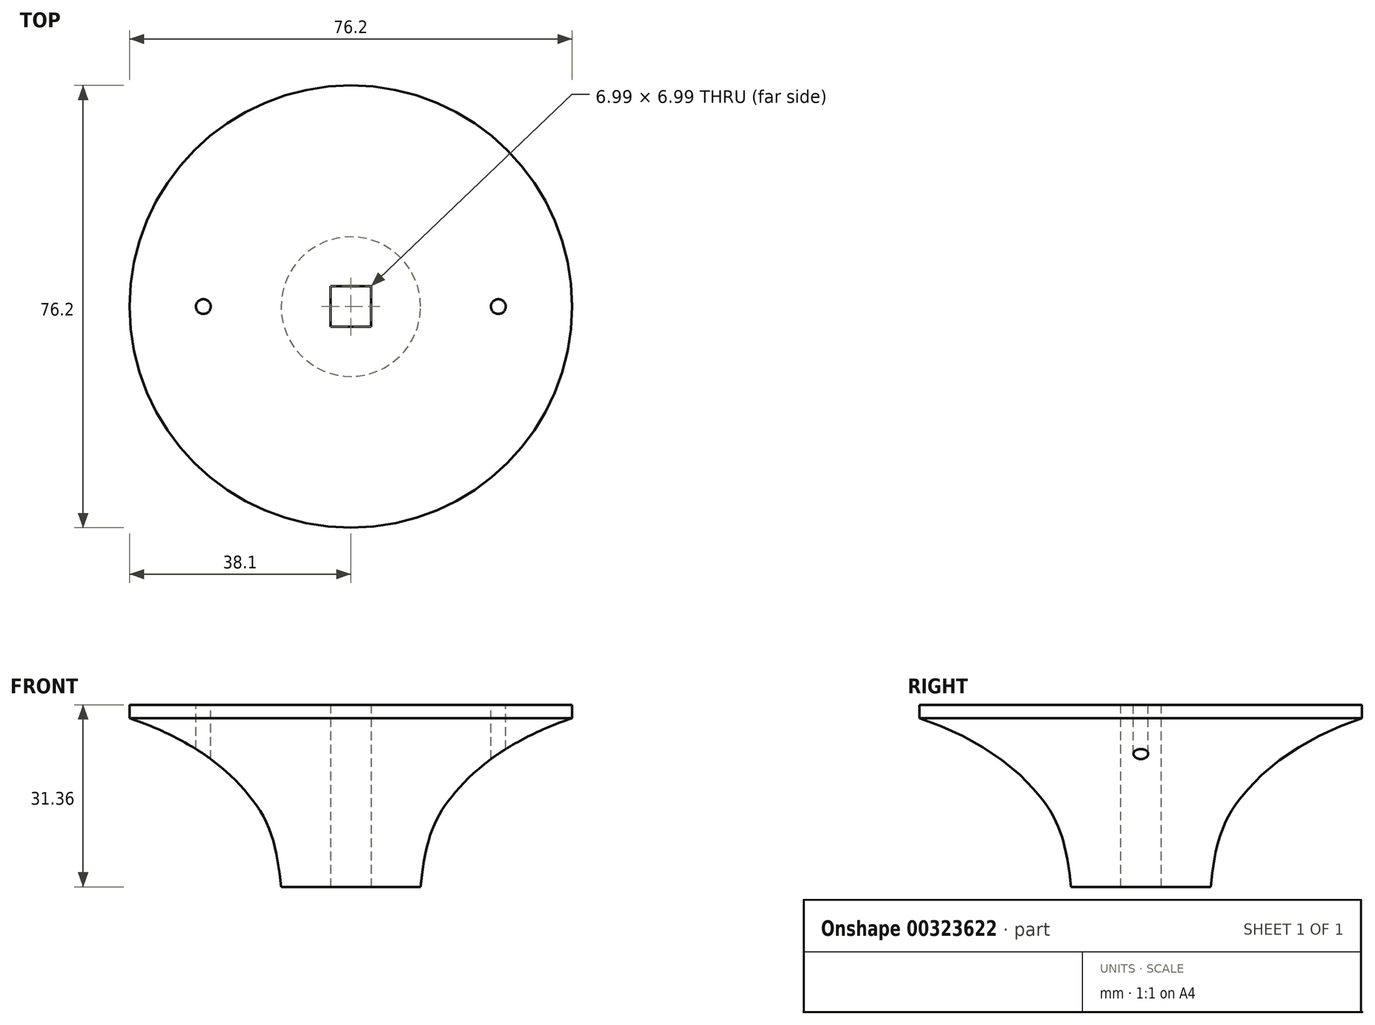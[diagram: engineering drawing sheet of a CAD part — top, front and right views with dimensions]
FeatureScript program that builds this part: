
annotation { "Feature Type Name" : "Feature", "Feature Type Description" : "" }
export const myFeature = defineFeature(function(context is Context, id is Id, definition is map)
    precondition{}
    {
        {
            var Q0;
            Q0=qCreatedBy(makeId("Right.planeOp"),FACE);
            var sketch = newSketch(context, id + "F0", { "sketchPlane" : qUnion([Q0])});
            skLineSegment(sketch, "E0", {"start": v(0, 31.36) * mm, "end": v(0, 0) * mm});
            skLineSegment(sketch, "E1", {"start": v(0, 31.36) * mm, "end": v(-38.1, 31.36) * mm});
            skLineSegment(sketch, "E2", {"start": v(-12.01, 0) * mm, "end": v(0, 0) * mm});
            skFitSpline(sketch, "E3", {"points": [v(-46.06, 31.36) * mm, v(-17.31, 15.47) * mm, v(-12.01, 0) * mm], "startDerivative": vector(85.22, -20.36) * mm, "endDerivative": vector(6.09, -59.35) * mm});
            skLineSegment(sketch, "E4", {"start": v(-38.1, 31.36) * mm, "end": v(-38.1, 29.06) * mm});
            skSolve(sketch);
        }
        {
            var Q0;
            Q0=makeQuery(id+"F0.imprint","IMPRINT",FACE,{"disambiguationData":[TD([[makeQuery(id+"F0.imprint","IMPRINT",EDGE,{"derivedFrom":sQuery(id+"F0.wireOp",EDGE,"E0")}),-1.0]])]});
            var Q1;
            Q1=sQuery(id+"F0.wireOp",EDGE,"E0");
            revolve(context, id + "F1", {"entities" : qUnion([Q0]), "axis" : qUnion([Q1]), "revolveType" : RevolveType.FULL});
        }
        {
            var Q0;
            Q0=qCreatedBy(makeId("Top.planeOp"),FACE);
            var sketch = newSketch(context, id + "F2", { "sketchPlane" : qUnion([Q0])});
            skLineSegment(sketch, "E5.bottom", {"start": v(-3.5, 3.5) * mm, "end": v(3.5, 3.5) * mm});
            skLineSegment(sketch, "E5.top", {"start": v(-3.5, -3.5) * mm, "end": v(3.5, -3.5) * mm});
            skLineSegment(sketch, "E5.left", {"start": v(-3.5, 3.5) * mm, "end": v(-3.5, -3.5) * mm});
            skLineSegment(sketch, "E5.right", {"start": v(3.5, 3.5) * mm, "end": v(3.5, -3.5) * mm});
            skPoint(sketch, "E5.middle", {"position": v(0, 0) * mm});
            skSolve(sketch);
        }
        {
            var Q0;
            Q0 = qSketchRegion(id + "F2", true);
            extrude(context, id + "F3", {"entities" : qUnion([Q0]), "operationType" : NewBodyOperationType.REMOVE, "endBound" : BoundingType.THROUGH_ALL, "depth" : 25.4 * mm});
        }
        {
            var Q0;
            Q0=makeQuery(id+"F1.opRevolve","SWEPT_FACE",FACE,{"disambiguationData":[OSD([sQuery(id+"F0.wireOp",EDGE,"E1")])]});
            var sketch = newSketch(context, id + "F4", { "sketchPlane" : qUnion([Q0])});
            skCircle(sketch, "E6", {"center": v(-25.4, 0) * mm, "radius": 1.27 * mm});
            skCircle(sketch, "E7", {"center": v(25.4, 0) * mm, "radius": 1.27 * mm});
            skSolve(sketch);
        }
        {
            var Q0;
            Q0 = qSketchRegion(id + "F4", true);
            extrude(context, id + "F5", {"entities" : qUnion([Q0]), "operationType" : NewBodyOperationType.REMOVE, "endBound" : BoundingType.THROUGH_ALL, "oppositeDirection" : true, "depth" : 25.4 * mm});
        }
    });
